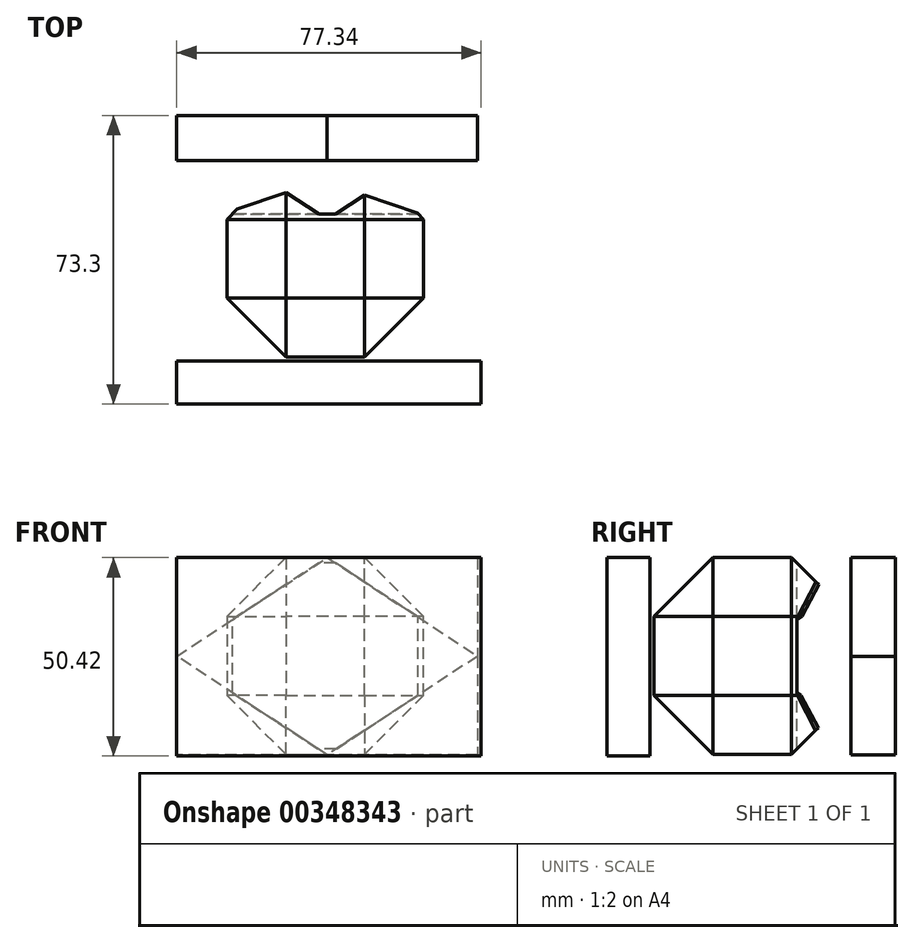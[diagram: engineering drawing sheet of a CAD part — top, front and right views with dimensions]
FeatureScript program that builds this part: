
annotation { "Feature Type Name" : "Feature", "Feature Type Description" : "" }
export const myFeature = defineFeature(function(context is Context, id is Id, definition is map)
    precondition{}
    {
        {
            var Q0;
            Q0=qCreatedBy(makeId("Front.planeOp"),FACE);
            var sketch = newSketch(context, id + "F0", { "sketchPlane" : qUnion([Q0])});
            skLineSegment(sketch, "E0.bottom", {"start": v(0, 0) * mm, "end": v(50, 0) * mm});
            skLineSegment(sketch, "E0.top", {"start": v(0, -50) * mm, "end": v(50, -50) * mm});
            skLineSegment(sketch, "E0.left", {"start": v(0, 0) * mm, "end": v(0, -50) * mm});
            skLineSegment(sketch, "E0.right", {"start": v(50, 0) * mm, "end": v(50, -50) * mm});
            skSolve(sketch);
        }
        {
            var Q0;
            Q0=makeQuery(id+"F0.imprint","IMPRINT",FACE,{"disambiguationData":[TD([[makeQuery(id+"F0.imprint","IMPRINT",EDGE,{"derivedFrom":sQuery(id+"F0.wireOp",EDGE,"E0.bottom")}),-1.0]])]});
            extrude(context, id + "F1", {"entities" : qUnion([Q0]), "depth" : 50 * mm});
        }
        {
            var Q0;
            Q0=makeQuery(id+"F1.opExtrude","SWEPT_FACE",FACE,{"disambiguationData":[OSD([sQuery(id+"F0.wireOp",EDGE,"E0.top")])]});
            var Q1;
            Q1=makeQuery(id+"F1.opExtrude","SWEPT_FACE",FACE,{"disambiguationData":[OSD([sQuery(id+"F0.wireOp",EDGE,"E0.right")])]});
            var Q2;
            Q2=makeQuery(id+"F1.opExtrude","CAP_FACE",FACE,{"disambiguationData":[OSD([sQuery(id+"F0.wireOp",EDGE,"E0.bottom"),sQuery(id+"F0.wireOp",EDGE,"E0.top"),sQuery(id+"F0.wireOp",EDGE,"E0.left"),sQuery(id+"F0.wireOp",EDGE,"E0.right")])],"isStart":false});
            var Q3;
            Q3=makeQuery(id+"F1.opExtrude","SWEPT_FACE",FACE,{"disambiguationData":[OSD([sQuery(id+"F0.wireOp",EDGE,"E0.bottom")])]});
            var Q4;
            Q4=makeQuery(id+"F1.opExtrude","SWEPT_FACE",FACE,{"disambiguationData":[OSD([sQuery(id+"F0.wireOp",EDGE,"E0.left")])]});
            chamfer(context, id + "F2", {"entities" : qUnion([Q0, Q1, Q2, Q3, Q4]), "width" : 15 * mm, "tangentPropagation" : true});
        }
        {
            var Q0;
            Q0=qCreatedBy(makeId("Front.planeOp"),FACE);
            cPlane(context, id + "F3", {"entities" : qUnion([Q0]), "cplaneType" : CPlaneType.OFFSET, "offset" : 51 * mm, "width" : 150 * mm, "height" : 150 * mm});
        }
        {
            var Q0;
            Q0=qCreatedBy(makeId("Front.planeOp"),FACE);
            var sketch = newSketch(context, id + "F4", { "sketchPlane" : qUnion([Q0])});
            skLineSegment(sketch, "E1.bottom", {"start": v(63.74, 0) * mm, "end": v(-12.75, 0) * mm});
            skLineSegment(sketch, "E1.top", {"start": v(63.74, -50.14) * mm, "end": v(-12.75, -50.14) * mm});
            skLineSegment(sketch, "E1.left", {"start": v(63.74, 0) * mm, "end": v(63.74, -50.14) * mm});
            skLineSegment(sketch, "E1.right", {"start": v(-12.75, 0) * mm, "end": v(-12.75, -50.14) * mm});
            skSolve(sketch);
        }
        {
            var Q0;
            Q0=qCreatedBy(id+"F3.planeOp",FACE);
            var sketch = newSketch(context, id + "F5", { "sketchPlane" : qUnion([Q0])});
            skLineSegment(sketch, "E2.bottom", {"start": v(-12.75, 0) * mm, "end": v(64.59, 0) * mm});
            skLineSegment(sketch, "E2.top", {"start": v(-12.75, -50.42) * mm, "end": v(64.59, -50.42) * mm});
            skLineSegment(sketch, "E2.left", {"start": v(-12.75, 0) * mm, "end": v(-12.75, -50.42) * mm});
            skLineSegment(sketch, "E2.right", {"start": v(64.59, 0) * mm, "end": v(64.59, -50.42) * mm});
            skSolve(sketch);
        }
        {
            var Q0;
            Q0 = qSketchRegion(id + "F4", true);
            extrude(context, id + "F6", {"entities" : qUnion([Q0]), "operationType" : NewBodyOperationType.ADD, "oppositeDirection" : true, "depth" : 11.4 * mm});
        }
        {
            var Q0;
            Q0 = qSketchRegion(id + "F5", true);
            extrude(context, id + "F7", {"entities" : qUnion([Q0]), "depth" : 10.9 * mm});
        }
        {
            var Q0;
            Q0=makeQuery(id+"F6.opExtrude","CAP_FACE",FACE,{"disambiguationData":[OSD([sQuery(id+"F4.wireOp",EDGE,"E1.bottom"),sQuery(id+"F4.wireOp",EDGE,"E1.top"),sQuery(id+"F4.wireOp",EDGE,"E1.left"),sQuery(id+"F4.wireOp",EDGE,"E1.right")])],"isStart":false});
            var sketch = newSketch(context, id + "F8", { "sketchPlane" : qUnion([Q0])});
            skLineSegment(sketch, "E3", {"start": v(-63.74, -25.07) * mm, "end": v(-25.5, 0) * mm});
            skLineSegment(sketch, "E4", {"start": v(-25.5, 0) * mm, "end": v(12.75, -25.07) * mm});
            skLineSegment(sketch, "E5", {"start": v(12.75, -25.07) * mm, "end": v(-25.5, -50.14) * mm});
            skLineSegment(sketch, "E6", {"start": v(-25.5, -50.14) * mm, "end": v(-63.74, -25.07) * mm});
            skLineSegment(sketch, "E7", {"start": v(12.75, -25.07) * mm, "end": v(-25.5, 0) * mm});
            skLineSegment(sketch, "E8", {"start": v(-63.74, -25.07) * mm, "end": v(-25.5, -50.14) * mm});
            skSolve(sketch);
        }
        {
            var Q0;
            Q0=makeQuery(id+"F8.imprint","IMPRINT",FACE,{"disambiguationData":[TD([[makeQuery(id+"F8.imprint","IMPRINT",EDGE,{"derivedFrom":sQuery(id+"F8.wireOp",EDGE,"E3")}),-1.0]])]});
            extrude(context, id + "F9", {"entities" : qUnion([Q0]), "operationType" : NewBodyOperationType.REMOVE, "oppositeDirection" : true, "depth" : 25 * mm});
        }
    });
